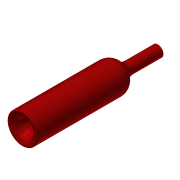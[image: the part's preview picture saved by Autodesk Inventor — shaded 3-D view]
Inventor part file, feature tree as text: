
AUTODESK INVENTOR PART (.ipt)
format: ipt  version: 2018 (Build 220112000, 112)  size: 154,112 bytes
history: native  units: mm
features: revolve x1, reference x1
ambient origin geometry x8: Origin, YZ Plane, XZ Plane, XY Plane, X Axis, Y Axis, Z Axis, Center Point
bodies: Solid1 (feature_tree)
feature tree (2):
  revolve  "Revolution1"  Angle=90.0deg
  reference  "Reference1"
